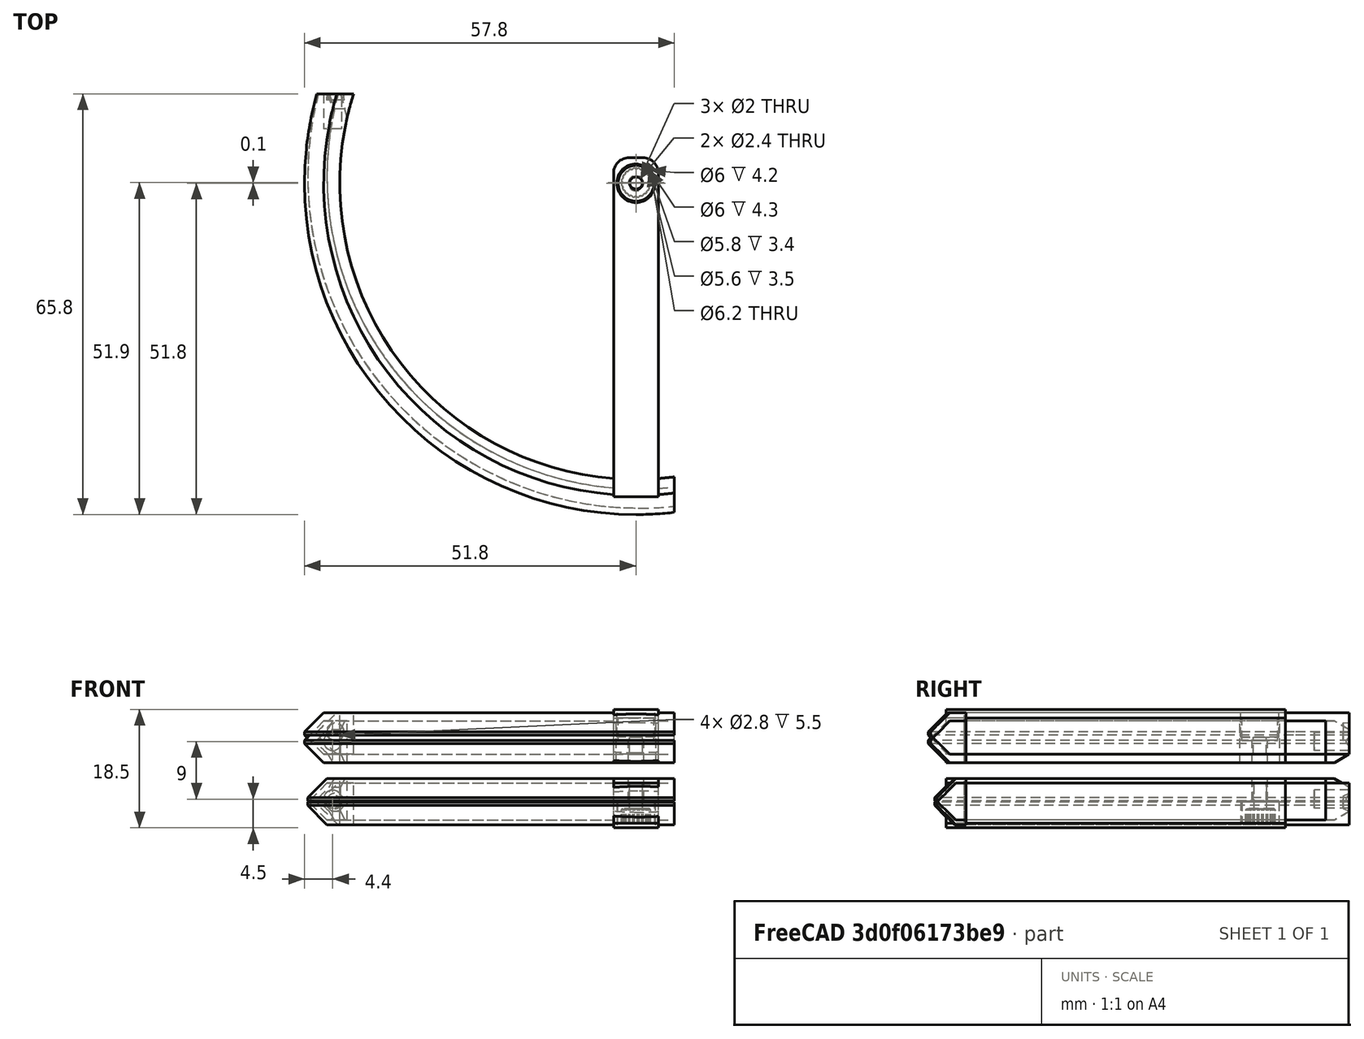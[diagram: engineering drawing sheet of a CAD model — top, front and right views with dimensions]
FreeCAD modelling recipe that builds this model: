
FCSTD DOCUMENT  (FreeCAD 0.15R4671 (Git))
Label: hopper_arms
License: All rights reserved
LicenseURL: http://en.wikipedia.org/wiki/All_rights_reserved
objects: Part::Cut×33, Part::Cylinder×21, Part::Box×18, Part::MultiFuse×10, Part::Feature×4, Part::Cone×4, Part::Chamfer×4, Part::Fillet×4, Part::MultiCommon×4, Mesh::Feature×2, Sketcher::SketchObject×1, App::MeasureDistance×1, PartDesign::Pocket×1
note: 105 computed .brp shape members not serialized (recipe doc carries the construction recipe); baked Part::Feature solids carry a one-line shape summary decoded from their .brp

FEATURE [Part::Feature] Fusion007001  label="Servo-sg90-final_donotprint"
  Placement = pos=(16.5,-2,-36.1) rot=(0,0,1;1.5708rad)
  shape: bbox 32.4 x 11.8 x 29.9 mm, 77 faces (baked)
FEATURE [Part::Feature] Fusion007005  label="Servo-sg90-final001_donotprint"
  Placement = pos=(16.5,-2,35.5) rot=(0.707107,-0.707107,0;3.14159rad)
  shape: bbox 32.4 x 11.8 x 29.9 mm, 77 faces (baked)
FEATURE [Part::Cone] Cone005
  Angle = 360
  Height = 6
  Placement = pos=(-47,11,-4.5) rot=(-1,0,0;1.5708rad)
  Radius1 = 1.4
  Radius2 = 1.4
FEATURE [Part::Cylinder] Cylinder019  label="pinion_donotprint001"
  Angle = 360
  Height = 15
  Placement = pos=(0,-2,-7) rot=(0,0,1;0rad)
  Radius = 1
FEATURE [Part::Box] Box011  label="Cube010"
  Height = 7
  Length = 53
  Placement = pos=(-4,-3.5,0) rot=(0,0,1;0rad)
  Width = 7
FEATURE [Part::Cylinder] Cylinder020
  Angle = 360
  Height = 6.5
  Placement = pos=(2,-8,0) rot=(0,0,1;0rad)
  Radius = 51.8
FEATURE [Part::Chamfer] Chamfer002
  Base = -> Cylinder020
  Edges = 2 edges r=3: [Edge1,Edge3]
FEATURE [Part::Fillet] Fillet002
  Base = -> Box011
  Edges = 2 edges r=2.4: [Edge1,Edge3]
  Placement = pos=(2,-8,0) rot=(0,0,1;0rad)
FEATURE [Part::Cylinder] Cylinder021
  Angle = 360
  Height = 7
  Placement = pos=(2,-8,0) rot=(0,0,1;0rad)
  Radius = 46.3
FEATURE [Part::Cut] Cut027
  Base = -> Chamfer002
  Tool = -> Cylinder021
FEATURE [Part::MultiFuse] Fusion007018
  Placement = pos=(-2,6,0) rot=(0,0,1;0rad)
  Shapes = -> [Cut027,Fillet002]
FEATURE [Part::Box] Box  label="Cube"
  Height = 10
  Length = 66
  Placement = pos=(-14,-59,-1) rot=(0,0,1;0rad)
  Width = 63
FEATURE [Part::MultiCommon] Common  label="armL"
  Placement = pos=(0,0,1) rot=(0,0,1;0rad)
  Shapes = -> [Fusion007018,Box]
FEATURE [Part::Cylinder] Cylinder022
  Angle = 360
  Height = 7.4
  Placement = pos=(2,-8,0) rot=(0,0,1;0rad)
  Radius = 46.3
FEATURE [Part::Box] Box014  label="Cube013"
  Height = 7
  Length = 53
  Placement = pos=(-4,-3.5,-0.5) rot=(0,0,1;0rad)
  Width = 7
FEATURE [Part::Fillet] Fillet003
  Base = -> Box014
  Edges = 2 edges r=2.4: [Edge1,Edge3]
  Placement = pos=(2,-8,0) rot=(0,0,1;0rad)
FEATURE [Part::Cylinder] Cylinder023
  Angle = 360
  Height = 6.5
  Placement = pos=(1,-7.5,0) rot=(0,0,1;0rad)
  Radius = 51.8
FEATURE [Part::Chamfer] Chamfer003
  Base = -> Cylinder023
  Edges = 2 edges r=3: [Edge1,Edge3]
FEATURE [Part::Cut] Cut028
  Base = -> Chamfer003
  Tool = -> Cylinder022
FEATURE [Part::MultiFuse] Fusion007019
  Placement = pos=(-2,6,0) rot=(0,0,1;0rad)
  Shapes = -> [Cut028,Fillet003]
FEATURE [Part::Box] Box015  label="Cube014"
  Height = 10
  Length = 66
  Placement = pos=(-14,-59,-1) rot=(0,0,1;0rad)
  Width = 63
FEATURE [Part::MultiCommon] Common002  label="armR"
  Placement = pos=(0,0,-8) rot=(0,0,1;0rad)
  Shapes = -> [Fusion007019,Box015]
FEATURE [Part::Cut] Cut030
  Base = -> Common002
  Tool = -> Fusion007001
FEATURE [Part::Cut] Cut031
  Base = -> Common
  Tool = -> Fusion007005
FEATURE [Part::Cut] Cut032  label="armL001"
  Base = -> Cut030
  Placement = pos=(2,-2,0) rot=(0,0,-1;1.5708rad)
  Tool = -> Cylinder019
FEATURE [Part::Cut] Cut033  label="armR001"
  Base = -> Cut031
  Placement = pos=(2,-2,0) rot=(0,0,-1;1.5708rad)
  Tool = -> Cylinder019
FEATURE [Part::Cone] Cone006
  Angle = 360
  Height = 5
  Placement = pos=(-47,11,4.5) rot=(-1,0,0;1.5708rad)
  Radius1 = 1.4
  Radius2 = 1.4
FEATURE [Part::Cone] Cone
  Angle = 360
  Height = 10
  Placement = pos=(-47,12,4.5) rot=(1,0,0;1.5708rad)
  Radius1 = 1.5
  Radius2 = 5
FEATURE [Part::Cut] Cut035
  Base = -> Cut033
  Tool = -> Cone006
FEATURE [Part::Cylinder] Cylinder
  Angle = 360
  Height = 10
  Placement = pos=(-47,2,4.5) rot=(-1,0,0;1.5708rad)
  Radius = 5
FEATURE [Part::Cut] Cut036
  Base = -> Cylinder
  Tool = -> Cone
FEATURE [Part::Cone] Cone007
  Angle = 360
  Height = 10
  Placement = pos=(-47,12,4.5) rot=(1,0,0;1.5708rad)
  Radius1 = 1.5
  Radius2 = 5
FEATURE [Part::Cylinder] Cylinder027
  Angle = 360
  Height = 10
  Placement = pos=(-47,2,4.5) rot=(-1,0,0;1.5708rad)
  Radius = 5
FEATURE [Part::Cut] Cut037
  Base = -> Cylinder027
  Placement = pos=(0,0,-9) rot=(0,0,1;0rad)
  Tool = -> Cone007
FEATURE [Part::Cut] Cut038  label="armL002"
  Base = -> Cut035
  Placement = pos=(0,0,1.3) rot=(0,0,1;0rad)
  Tool = -> Cut036
FEATURE [Part::Cut] Cut039
  Base = -> Cut032
  Tool = -> Cone005
FEATURE [Part::Cut] Cut040  label="armR002"
  Base = -> Cut039
  Placement = pos=(0,0,-0.7) rot=(0,0,1;0rad)
  Tool = -> Cut037
FEATURE [Part::Cylinder] Cylinder099
  Angle = 360
  Height = 10
  Placement = pos=(0,-2,5) rot=(0,0,1;0rad)
  Radius = 3
FEATURE [Part::Box] Box150  label="Cube135"
  Height = 30
  Length = 30
  Placement = pos=(-10.2,-8,10) rot=(0,0,1;0rad)
  Width = 12
FEATURE [Part::MultiFuse] Fusion007074  label="hs-82mg002"
  Placement = pos=(0,-4,0) rot=(1,0,0;3.14159rad)
  Shapes = -> [Box150,Cylinder099]
FEATURE [Part::Cylinder] Cylinder100
  Angle = 360
  Height = 10
  Placement = pos=(0,-2,5) rot=(0,0,1;0rad)
  Radius = 3
FEATURE [Part::Box] Box151  label="Cube136"
  Height = 30
  Length = 30
  Placement = pos=(-10.2,-8,10) rot=(0,0,1;0rad)
  Width = 12
FEATURE [Part::MultiFuse] Fusion007075  label="hs-82mg003"
  Shapes = -> [Box151,Cylinder100]
FEATURE [Part::MultiFuse] Fusion007076  label="2Hs-82mg001"
  Shapes = -> [Fusion007075,Fusion007074]
FEATURE [Part::Cylinder] Cylinder101
  Angle = 360
  Height = 10
  Placement = pos=(0,-2,5) rot=(0,0,1;0rad)
  Radius = 3
FEATURE [Part::Box] Box152  label="Cube137"
  Height = 30
  Length = 30
  Placement = pos=(-10.2,-8,10) rot=(0,0,1;0rad)
  Width = 12
FEATURE [Part::MultiFuse] Fusion007078  label="hs-82mg004"
  Placement = pos=(0,-4,0) rot=(1,0,0;3.14159rad)
  Shapes = -> [Box152,Cylinder101]
FEATURE [Part::Box] Box153  label="Cube138"
  Height = 30
  Length = 30
  Placement = pos=(-10.2,-8,10) rot=(0,0,1;0rad)
  Width = 12
FEATURE [Part::Cylinder] Cylinder102
  Angle = 360
  Height = 10
  Placement = pos=(0,-2,5) rot=(0,0,1;0rad)
  Radius = 3
FEATURE [Part::MultiFuse] Fusion007079  label="hs-82mg005"
  Shapes = -> [Box153,Cylinder102]
FEATURE [Part::MultiFuse] Fusion007077  label="2Hs-82mg002"
  Shapes = -> [Fusion007079,Fusion007078]
FEATURE [Part::Cut] Cut118  label="armR13b"
  Base = -> Cut040
  Tool = -> Fusion007076
FEATURE [Part::Cut] Cut119  label="armL13b"
  Base = -> Cut038
  Tool = -> Fusion007077
FEATURE [Part::Cylinder] Cylinder103
  Angle = 360
  Height = 7
  Placement = pos=(2,-8,0) rot=(0,0,1;0rad)
  Radius = 46.3
FEATURE [Part::Cylinder] Cylinder104  label="pinion_donotprint002"
  Angle = 360
  Height = 15
  Placement = pos=(0,-2,-7) rot=(0,0,1;0rad)
  Radius = 1
FEATURE [Part::Cylinder] Cylinder105
  Angle = 360
  Height = 6.5
  Placement = pos=(2,-8,0) rot=(0,0,1;0rad)
  Radius = 51.8
FEATURE [Part::Box] Box154  label="Cube139"
  Height = 7
  Length = 53
  Placement = pos=(-4,-3.5,0) rot=(0,0,1;0rad)
  Width = 7
FEATURE [Part::Fillet] Fillet004
  Base = -> Box154
  Edges = 2 edges r=2.4: [Edge1,Edge3]
  Placement = pos=(2,-8,0) rot=(0,0,1;0rad)
FEATURE [Part::Box] Box155  label="Cube140"
  Height = 10
  Length = 66
  Placement = pos=(-14,-59,-1) rot=(0,0,1;0rad)
  Width = 63
FEATURE [Part::Chamfer] Chamfer004
  Base = -> Cylinder105
  Edges = 2 edges r=3: [Edge1,Edge3]
FEATURE [Part::Cut] Cut122
  Base = -> Chamfer004
  Tool = -> Cylinder103
FEATURE [Part::MultiFuse] Fusion007080
  Placement = pos=(-2,6,0) rot=(0,0,1;0rad)
  Shapes = -> [Cut122,Fillet004]
FEATURE [Part::MultiCommon] Common003  label="armL003"
  Placement = pos=(0,0,1) rot=(0,0,1;0rad)
  Shapes = -> [Fusion007080,Box155]
FEATURE [Part::Feature] Fusion007081  label="Servo-sg90-final001_donotprint001"
  Placement = pos=(16.5,-2,35.5) rot=(0.707107,-0.707107,0;3.14159rad)
  shape: bbox 32.4 x 11.8 x 29.9 mm, 77 faces (baked)
FEATURE [Part::Cut] Cut121
  Base = -> Common003
  Tool = -> Fusion007081
FEATURE [Part::Cut] Cut120  label="armR003"
  Base = -> Cut121
  Placement = pos=(2,-2,0) rot=(0,0,-1;1.5708rad)
  Tool = -> Cylinder104
FEATURE [Part::Cylinder] Cylinder106
  Angle = 360
  Height = 6
  Placement = pos=(-47.4,12.5,4.3) rot=(1,0,0;1.5708rad)
  Radius = 1.4
FEATURE [Part::Box] Box156  label="Cube141"
  Height = 10
  Length = 10
  Placement = pos=(-44,4,0) rot=(0,0,1;0.261799rad)
  Width = 10
FEATURE [Part::Cylinder] Cylinder108  label="pinion_donotprint003"
  Angle = 360
  Height = 15
  Placement = pos=(-0.1,-2,-12) rot=(0,0,1;0rad)
  Radius = 1
FEATURE [Part::Cylinder] Cylinder109
  Angle = 360
  Height = 6.5
  Placement = pos=(1,-7.5,0) rot=(0,0,1;0rad)
  Radius = 51.8
FEATURE [Part::Chamfer] Chamfer006
  Base = -> Cylinder109
  Edges = 2 edges r=3: [Edge1,Edge3]
FEATURE [Part::Cylinder] Cylinder110
  Angle = 360
  Height = 7.4
  Placement = pos=(2,-8,0) rot=(0,0,1;0rad)
  Radius = 46.3
FEATURE [Part::Cut] Cut125
  Base = -> Chamfer006
  Tool = -> Cylinder110
FEATURE [Part::Box] Box157  label="Cube142"
  Height = 7
  Length = 53
  Placement = pos=(-4,-3.5,-0.5) rot=(0,0,1;0rad)
  Width = 7
FEATURE [Part::Fillet] Fillet005
  Base = -> Box157
  Edges = 2 edges r=2.4: [Edge1,Edge3]
  Placement = pos=(2,-8,0) rot=(0,0,1;0rad)
FEATURE [Part::MultiFuse] Fusion007082
  Placement = pos=(-2,6,0) rot=(0,0,1;0rad)
  Shapes = -> [Cut125,Fillet005]
FEATURE [Part::Box] Box158  label="Cube143"
  Height = 10
  Length = 66
  Placement = pos=(-14,-59,-1) rot=(0,0,1;0rad)
  Width = 63
FEATURE [Part::MultiCommon] Common004  label="armR004"
  Placement = pos=(0,0,-8) rot=(0,0,1;0rad)
  Shapes = -> [Fusion007082,Box158]
FEATURE [Part::Feature] Fusion007083  label="Servo-sg90-final_donotprint001"
  Placement = pos=(16.5,-2,-36.1) rot=(0,0,1;1.5708rad)
  shape: bbox 32.4 x 11.8 x 29.9 mm, 77 faces (baked)
FEATURE [Part::Cut] Cut126
  Base = -> Common004
  Tool = -> Fusion007083
FEATURE [Part::Cut] Cut124  label="armL004"
  Base = -> Cut126
  Placement = pos=(2,-2,0) rot=(0,0,-1;1.5708rad)
  Tool = -> Cylinder108
FEATURE [Part::Cylinder] Cylinder111
  Angle = 360
  Height = 6
  Placement = pos=(-47.4,12.5,-4.7) rot=(1,0,0;1.5708rad)
  Radius = 1.4
FEATURE [Part::Box] Box159  label="Cube144"
  Height = 10
  Length = 10
  Placement = pos=(-44,4,-9) rot=(0,0,1;0.261799rad)
  Width = 10
FEATURE [Part::Cut] Cut127
  Base = -> Cut124
  Tool = -> Cylinder111
FEATURE [Part::Cut] Cut128  label="arm14L"
  Base = -> Cut127
  Tool = -> Box159
FEATURE [Part::Box] Box160  label="Cube145"
  Height = 4
  Length = 4
  Placement = pos=(-48,9,-13) rot=(1,0,0;0.523599rad)
  Width = 6
FEATURE [Part::Box] Box161  label="Cube146"
  Height = 4
  Length = 4
  Placement = pos=(-48,7,0) rot=(-1,0,0;0.523599rad)
  Width = 6
FEATURE [Part::Cut] Cut129
  Base = -> Cut128
  Tool = -> Box160
FEATURE [Part::Cut] Cut130  label="arm14la"
  Base = -> Cut129
  Tool = -> Box161
FEATURE [Part::Box] Box162  label="Cube147"
  Height = 4
  Length = 4
  Placement = pos=(-49,9,-4) rot=(1,0,0;0.523599rad)
  Width = 6
FEATURE [Part::Box] Box163  label="Cube148"
  Height = 4
  Length = 4
  Placement = pos=(-49,7,9) rot=(-1,0,0;0.523599rad)
  Width = 6
FEATURE [Sketcher::SketchObject] Sketch
  Placement = pos=(0,0,-8.5) rot=(1,0,0;3.14159rad)
  Support = -> Cut130 [Face20]
  sketch-geometry (1):
    g0: Circle CenterX=0 CenterY=1.90037 CenterZ=0 NormalX=0 NormalY=0 NormalZ=1 Radius=2.9
  constraints (2):
    c: DistanceX(g-1,g0) = 0
    c: Radius(g0) = 2.9
FEATURE [App::MeasureDistance] Distance  label="Distance: 6.994"
  Distance = 6.99365
  P1 = (3.5,-0.405981,-1.5)
  P2 = (3.5,-0.4,-8.49365)
FEATURE [PartDesign::Pocket] Pocket
  Length = 3.4
  Sketch = -> Sketch
  Type = 0
FEATURE [Part::Cylinder] Cylinder113
  Angle = 360
  Height = 50
  Placement = pos=(0,-2,-19) rot=(0,0,1;0rad)
  Radius = 1.2
FEATURE [Part::Cut] Cut134
  Base = -> Pocket
  Tool = -> Cylinder113
FEATURE [Part::Cut] Cut
  Base = -> Cut120
  Tool = -> Cylinder106
FEATURE [Part::Cut] Cut123  label="arm14R"
  Base = -> Cut
  Tool = -> Box156
FEATURE [Part::Cut] Cut131
  Base = -> Cut123
  Tool = -> Box162
FEATURE [Part::Cut] Cut132  label="arm14ra"
  Base = -> Cut131
  Tool = -> Box163
FEATURE [Part::Cylinder] Cylinder112
  Angle = 360
  Height = 40
  Placement = pos=(0,-2,4.5) rot=(0,0,1;0rad)
  Radius = 2.8
FEATURE [Part::Cut] Cut133
  Base = -> Cut132
  Tool = -> Cylinder112
FEATURE [Part::Cut] Cut135
  Base = -> Cut133
FEATURE [Part::Cut] Cut136
  Base = -> Cut132
  Tool = -> Cylinder112
FEATURE [Part::Cut] Cut137
  Base = -> Cut136
  Tool = -> Cylinder113
FEATURE [Mesh::Feature] Mesh  label="left_arm"
FEATURE [Mesh::Feature] Mesh001  label="right_arm"
